# Revit family: Deca_Cuba de sobrepor retangular com mesa e válvula oculta_Cubas Espec._L.870
name_source: partatom
category: Plumbing Fixtures
units: mm (PartAtom-declared; Revit-internal decimal feet)

## family parameters
Cut with Voids When Loaded = Yes
Host = Face
Part Type = Normal
Room Calculation Point = No
Round Connector Dimension = Use Radius
Shared = No

## types (1)
- L.870.17_Branco
    Acompanha o Produto = -
    Aprovado por = quattroD
    Atendimento ao Cliente = 0800-0117073
    Categoria = CUBAS
    Composição Anel Vedação = -
    Composição Assento = -
    Composição Básica = Argila, feldspato, caulim, vidrados e corantes inorgânicos.
    Composição Componente = Liga de cobre (bronze e latão), elastômeros e plásticos de engenharia.
    Consumo = -
    Cor Interna = -
    Cor Principal = Branco
    Cor Secundária = -
    Cores Componente = Não Possui
    Criado por = quattroD
    Código Pai = L.870
    Default Elevation = 0 mm  [stored 0 ft]
    Description = Cuba de sobrepor retangular com mesa e válvula oculta
    Diâmetro Ponto de Esgoto = 25 mm  [stored 0.082021 ft]
    Informações Complementares = -
    Itens de Instalação = 1680.C.100.112; 1682.C.100.112; 1684.C.100.112
    Linha = Cubas Espec.
    Manufacturer = Deca
    Material = Deca_Branco
    Model = L.870.17
    Norma = NBR-16728-1;NBR-16728-2
    Peso Líquido (Kg) = 18.263
    Pressão máx. funcionamento = -
    Pressão mín. Aquec. Acúmulo = -
    Pressão mín. Aquec. Passagem = -
    Pressão mín. funcionamento = -
    Raio Ponto de Esgoto = 13 mm  [stored 0.0426509 ft]
    Saída de Esgoto = Válvula Oculta
    Segmento = Banheiro Luxo
    Tipo de dispositivo economizador = -
    Tipo de mecanismo utilizado = -
    Tipo de rosca de entrada = -
    Tipo de rosca de saída = -
    URL = www.deca.com.br
    Vazão na Pressão máx. (L/min) = -
    Vazão na Pressão mín. (L/min) = -

note: [stored X ft] marks values corroborated as IEEE doubles in the binary element streams (Revit-internal decimal feet)

## geometry (parser evidence)
native form markers: Sweep x3
no freeform markers — native parametric forms only
